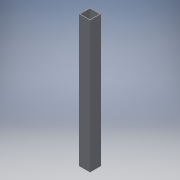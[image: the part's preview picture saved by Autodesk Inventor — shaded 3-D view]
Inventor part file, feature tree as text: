
AUTODESK INVENTOR PART (.ipt)
format: ipt  version: 2016 (Build 200138000, 138)  size: 104,960 bytes
history: native  units: in
note: dims shown in document units (in); Inventor stores cm internally (conversion verified against a paired STEP export)
features: extrude x2, sketch x2
ambient origin geometry x8: Origin, YZ Plane, XZ Plane, XY Plane, X Axis, Y Axis, Z Axis, Center Point
bodies: Solid1 (feature_tree)
feature tree (4):
  extrude  "Extrusion1"  Depth=1.0in
  extrude  "Extrusion2"  Depth=1.0in TaperAngle=0.0deg
  sketch  "Sketch1"  dims[d0=1.0in d1=1.0in]
  sketch  "Sketch2"  dims[d2=0.0625in d3=9.3708in d4=0.0in d5=0.3018in d6=1.0in d7=0.0in]
